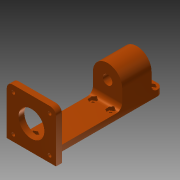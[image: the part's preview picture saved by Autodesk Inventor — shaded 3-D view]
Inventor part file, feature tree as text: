
AUTODESK INVENTOR PART (.ipt)
format: ipt  version: 2013 (Build 170138000, 138)  size: 259,584 bytes
history: native  units: mm
features: extrude x8, sketch x8, projected_geometry x4, fillet x2
ambient origin geometry x8: Origin, YZ Plane, XZ Plane, XY Plane, X Axis, Y Axis, Z Axis, Center Point
bodies: Solid1 (feature_tree)
feature tree (22):
  extrude  "Extrusion1"  Depth=5.0mm TaperAngle=0.0deg
  extrude  "Extrusion2"  Depth=22.1mm
  extrude  "Extrusion3"  Depth=5.0mm TaperAngle=0.0deg
  extrude  "Extrusion7"  Depth=5.0mm
  extrude  "Extrusion8"  Depth=5.0mm TaperAngle=0.0deg
  extrude  "Extrusion9"  Depth=25.0mm TaperAngle=0.0deg
  extrude  "Extrusion10"  Depth=5.0mm
  extrude  "Extrusion11"  Depth=3.1mm
  fillet  "Fillet1"  Radius=2.5mm
  fillet  "Fillet2"  Radius=5.6mm
  sketch  "Sketch1"  dims[d0=42.0mm d2=5.0mm d3=0.0mm]
  sketch  "Sketch2"  dims[d4=31.0mm d5=22.1mm]
  sketch  "Sketch3"  dims[d6=3.1mm d7=5.0mm d8=0.0mm]
  sketch  "Sketch7"  dims[d9=25.0mm d11=5.0mm]
  sketch  "Sketch8"  dims[d12=60.0mm d13=0.0mm d23=5.0mm d24=0.0mm]
  projected_geometry  "Projected Loop3"
  sketch  "Sketch9"  dims[d25=8.1mm d27=25.0mm d28=0.0mm]
  sketch  "Sketch10"  dims[d29=10.0mm d30=0.0mm d31=5.0mm]
  projected_geometry  "Projected Loop4"
  projected_geometry  "Projected Loop5"
  sketch  "Sketch11"  dims[d32=5.0mm d33=3.1mm d34=2.5mm d35=0.0mm d36=5.6mm d37=2.5mm d38=0.0mm d39=5.0mm d40=5.0mm]
  projected_geometry  "Project Cut Edges1"
